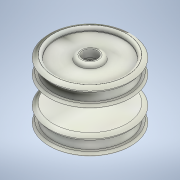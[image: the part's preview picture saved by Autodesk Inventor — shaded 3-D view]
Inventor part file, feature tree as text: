
AUTODESK INVENTOR PART (.ipt)
format: ipt  version: 2022 (Build 260153000, 153)  size: 297,984 bytes
history: native  units: mm
features: extrude x12, sketch x12, fillet x3, chamfer x1, mirror x1
ambient origin geometry x8: Origin, YZ Plane, XZ Plane, XY Plane, X Axis, Y Axis, Z Axis, Center Point
bodies: Solid1 (feature_tree)
feature tree (29):
  extrude  "Extrusion1"  Depth=4.0mm
  extrude  "Extrusion2"  Depth=4.0mm
  extrude  "Extrusion3"  Depth=2.0mm TaperAngle=0.0deg
  extrude  "Extrusion4"  TaperAngle=0.0deg  [1 undecoded]
  extrude  "Extrusion5"  Depth=4.0mm TaperAngle=0.0deg
  extrude  "Extrusion6"  Depth=2.0mm
  fillet  "Fillet1"  Radius=17.0mm
  chamfer  "Chamfer2"  [1 undecoded]
  extrude  "Extrusion7"  Depth=1.5mm
  mirror  "Mirror1"
  extrude  "Extrusion8"  Depth=6.0mm
  fillet  "Fillet2"  Radius=10.0mm
  fillet  "Fillet3"  Radius=1.5mm
  extrude  "Extrusion9"  Depth=4.0mm
  extrude  "Extrusion10"  Depth=5.0mm
  extrude  "Extrusion11"  Depth=6.0mm TaperAngle=0.0deg
  extrude  "Extrusion12"  Depth=6.0mm
  sketch  "Sketch1"  dims[d0=17.0mm d1=4.0mm]
  sketch  "Sketch2"  dims[d2=8.0mm d3=0.0mm d4=4.0mm]
  sketch  "Sketch3"  dims[d5=9.0mm d6=0.0mm d7=2.0mm d8=0.0mm]
  sketch  "Sketch4"  dims[d9=2.2mm d10=0.0mm d11=0.0mm]
  sketch  "Sketch5"  dims[d12=15.0mm d13=4.0mm d14=0.0mm]
  sketch  "Sketch6"  dims[d15=2.0mm d16=0.0mm d17=2.0mm]
  sketch  "Sketch7"  dims[d21=1.0mm d22=1.95mm d23=45.0deg d24=17.0mm d25=0.0mm d26=0.0mm]
  sketch  "Sketch8"  dims[d28=1.5mm d29=0.0mm d30=27.5mm]
  sketch  "Sketch9"  dims[d31=1.2mm d32=6.0mm d33=10.0mm d34=1.5mm]
  sketch  "Sketch10"  dims[d35=3.2mm d36=0.0mm d37=4.0mm]
  sketch  "Sketch11"  dims[d38=5.0mm d39=0.0mm d40=5.2mm]
  sketch  "Sketch12"  dims[d41=9.0mm d42=0.0mm d43=6.0mm d44=0.0mm d45=6.0mm]
note: 2 required parameter values undecoded (feature->parameter linkage not recoverable at this tier; creation-order binding heuristic only, values carry confidence <= 0.55)
